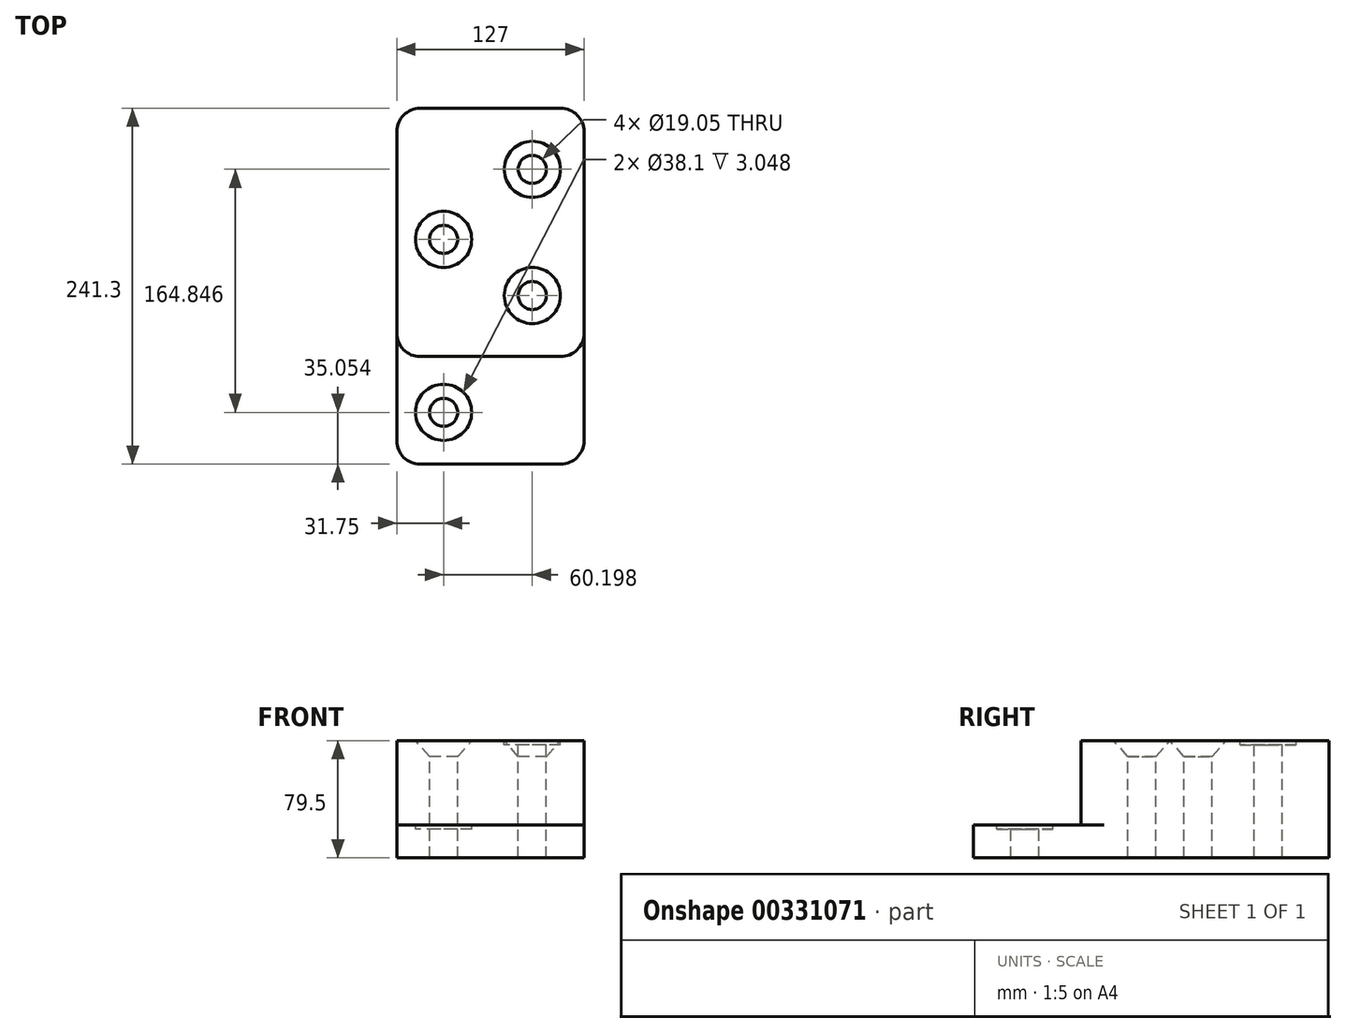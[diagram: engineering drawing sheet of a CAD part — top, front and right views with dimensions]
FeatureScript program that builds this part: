
annotation { "Feature Type Name" : "Feature", "Feature Type Description" : "" }
export const myFeature = defineFeature(function(context is Context, id is Id, definition is map)
    precondition{}
    {
        {
            var Q0;
            Q0=qCreatedBy(makeId("Top.planeOp"),FACE);
            var sketch = newSketch(context, id + "F0", { "sketchPlane" : qUnion([Q0])});
            skLineSegment(sketch, "E0", {"start": v(0, 0) * mm, "end": v(127, 0) * mm});
            skLineSegment(sketch, "E1", {"start": v(127, 0) * mm, "end": v(127, 168.4) * mm});
            skLineSegment(sketch, "E2", {"start": v(127, 168.4) * mm, "end": v(0, 168.4) * mm});
            skLineSegment(sketch, "E3", {"start": v(0, 168.4) * mm, "end": v(0, 0) * mm});
            skLineSegment(sketch, "E4", {"start": v(0, 0) * mm, "end": v(0, -72.9) * mm});
            skLineSegment(sketch, "E5", {"start": v(0, -72.9) * mm, "end": v(127, -72.9) * mm});
            skLineSegment(sketch, "E6", {"start": v(127, -72.9) * mm, "end": v(127, 0) * mm});
            skSolve(sketch);
        }
        {
            var Q0;
            Q0=makeQuery(id+"F0.imprint","IMPRINT",FACE,{"disambiguationData":[TD([[makeQuery(id+"F0.imprint","IMPRINT",EDGE,{"derivedFrom":sQuery(id+"F0.wireOp",EDGE,"E0")}),1.0]])]});
            extrude(context, id + "F1", {"entities" : qUnion([Q0]), "depth" : 79.5 * mm});
        }
        {
            var Q0;
            Q0=makeQuery(id+"F0.imprint","IMPRINT",FACE,{"disambiguationData":[TD([[makeQuery(id+"F0.imprint","IMPRINT",EDGE,{"derivedFrom":sQuery(id+"F0.wireOp",EDGE,"E0")}),-1.0]])]});
            extrude(context, id + "F2", {"entities" : qUnion([Q0]), "operationType" : NewBodyOperationType.ADD, "depth" : 22.35 * mm});
        }
        {
            var Q0;
            Q0=makeQuery(id+"F2.opExtrude","CAP_FACE",FACE,{"disambiguationData":[OSD([sQuery(id+"F0.wireOp",EDGE,"E0"),sQuery(id+"F0.wireOp",EDGE,"E4"),sQuery(id+"F0.wireOp",EDGE,"E5"),sQuery(id+"F0.wireOp",EDGE,"E6")])],"isStart":false});
            var sketch = newSketch(context, id + "F3", { "sketchPlane" : qUnion([Q0])});
            skCircle(sketch, "E7", {"center": v(31.75, -37.85) * mm, "radius": 9.53 * mm});
            skSolve(sketch);
        }
        {
            var Q0;
            Q0=sQuery(id+"F3.wireOp",VERTEX,"E7.center");
            var Q1;
            Q1=makeQuery(id+"F1.opExtrude","SWEPT_BODY",BODY,{"disambiguationData":[OSD([sQuery(id+"F0.wireOp",EDGE,"E0"),sQuery(id+"F0.wireOp",EDGE,"E1"),sQuery(id+"F0.wireOp",EDGE,"E2"),sQuery(id+"F0.wireOp",EDGE,"E3")])]});
            hole(context, id + "F4", {"style" : HoleStyle.C_BORE, "endStyle" : HoleEndStyle.THROUGH, "holeDiameter" : 19.05 * mm, "cBoreDiameter" : 38.1 * mm, "cBoreDepth" : 3.05 * mm, "tappedDepth" : 12.7 * mm, "tapClearance" : 3, "locations" : qUnion([Q0]), "scope" : qUnion([Q1])});
        }
        {
            var Q0;
            Q0=makeQuery(id+"F1.opExtrude","CAP_FACE",FACE,{"disambiguationData":[OSD([sQuery(id+"F0.wireOp",EDGE,"E0"),sQuery(id+"F0.wireOp",EDGE,"E1"),sQuery(id+"F0.wireOp",EDGE,"E2"),sQuery(id+"F0.wireOp",EDGE,"E3")])],"isStart":false});
            var sketch = newSketch(context, id + "F5", { "sketchPlane" : qUnion([Q0])});
            skCircle(sketch, "E8", {"center": v(91.95, 127) * mm, "radius": 9.53 * mm});
            skCircle(sketch, "E9", {"center": v(31.75, 79.5) * mm, "radius": 9.53 * mm});
            skCircle(sketch, "E10", {"center": v(91.95, 41.4) * mm, "radius": 9.53 * mm});
            skSolve(sketch);
        }
        {
            var Q0;
            Q0=sQuery(id+"F5.wireOp",VERTEX,"E8.center");
            var Q1;
            Q1=makeQuery(id+"F1.opExtrude","SWEPT_BODY",BODY,{"disambiguationData":[OSD([sQuery(id+"F0.wireOp",EDGE,"E0"),sQuery(id+"F0.wireOp",EDGE,"E1"),sQuery(id+"F0.wireOp",EDGE,"E2"),sQuery(id+"F0.wireOp",EDGE,"E3")])]});
            hole(context, id + "F6", {"style" : HoleStyle.C_BORE, "endStyle" : HoleEndStyle.THROUGH, "holeDiameter" : 19.05 * mm, "cBoreDiameter" : 38.1 * mm, "cBoreDepth" : 3.05 * mm, "tappedDepth" : 12.7 * mm, "tapClearance" : 3, "locations" : qUnion([Q0]), "scope" : qUnion([Q1])});
        }
        {
            var Q0;
            Q0=sQuery(id+"F5.wireOp",VERTEX,"E9.center");
            var Q1;
            Q1=sQuery(id+"F5.wireOp",VERTEX,"E10.center");
            var Q2;
            Q2=makeQuery(id+"F1.opExtrude","SWEPT_BODY",BODY,{"disambiguationData":[OSD([sQuery(id+"F0.wireOp",EDGE,"E0"),sQuery(id+"F0.wireOp",EDGE,"E1"),sQuery(id+"F0.wireOp",EDGE,"E2"),sQuery(id+"F0.wireOp",EDGE,"E3")])]});
            hole(context, id + "F7", {"style" : HoleStyle.C_SINK, "endStyle" : HoleEndStyle.THROUGH, "holeDiameter" : 19.05 * mm, "cSinkDiameter" : 38.1 * mm, "cSinkAngle" : 82 * degree, "tappedDepth" : 12.7 * mm, "tapClearance" : 3, "locations" : qUnion([Q0, Q1]), "scope" : qUnion([Q2])});
        }
        {
            var Q0;
            Q0=makeQuery(id+"F1.opExtrude","SWEPT_EDGE",EDGE,{"disambiguationData":[OSD([sQuery(id+"F0.wireOp",EDGE,"E0"),sQuery(id+"F0.wireOp",EDGE,"E1"),sQuery(id+"F0.wireOp",EDGE,"E6")])]});
            var Q1;
            Q1=makeQuery(id+"F2.opExtrude","SWEPT_EDGE",EDGE,{"disambiguationData":[OSD([sQuery(id+"F0.wireOp",EDGE,"E5"),sQuery(id+"F0.wireOp",EDGE,"E6")])]});
            var Q2;
            Q2=makeQuery(id+"F2.opExtrude","SWEPT_EDGE",EDGE,{"disambiguationData":[OSD([sQuery(id+"F0.wireOp",EDGE,"E4"),sQuery(id+"F0.wireOp",EDGE,"E5")])]});
            var Q3;
            Q3=makeQuery(id+"F1.opExtrude","SWEPT_EDGE",EDGE,{"disambiguationData":[OSD([sQuery(id+"F0.wireOp",EDGE,"E0"),sQuery(id+"F0.wireOp",EDGE,"E3"),sQuery(id+"F0.wireOp",EDGE,"E4")])]});
            var Q4;
            Q4=makeQuery(id+"F1.opExtrude","SWEPT_EDGE",EDGE,{"disambiguationData":[OSD([sQuery(id+"F0.wireOp",EDGE,"E1"),sQuery(id+"F0.wireOp",EDGE,"E2")])]});
            var Q5;
            Q5=makeQuery(id+"F1.opExtrude","SWEPT_EDGE",EDGE,{"disambiguationData":[OSD([sQuery(id+"F0.wireOp",EDGE,"E2"),sQuery(id+"F0.wireOp",EDGE,"E3")])]});
            fillet(context, id + "F8", {"entities" : qUnion([Q0, Q1, Q2, Q3, Q4, Q5]), "radius" : 15.75 * mm, "tangentPropagation" : true, "allowEdgeOverflow" : false});
        }
    });
